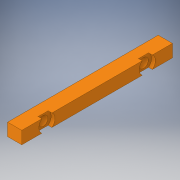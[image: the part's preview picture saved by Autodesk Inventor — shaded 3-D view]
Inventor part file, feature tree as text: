
AUTODESK INVENTOR PART (.ipt)
format: ipt  version: 2019 (Build 230136000, 136)  size: 123,904 bytes
history: native  units: in
note: dims shown in document units (in); Inventor stores cm internally (conversion verified against a paired STEP export)
features: sketch x3, extrude x2, hole x1
ambient origin geometry x8: Origin, YZ Plane, XZ Plane, XY Plane, X Axis, Y Axis, Z Axis, Center Point
bodies: Solid1 (feature_tree)
feature tree (6):
  extrude  "Extrusion1"  Depth=0.565in
  extrude  "Extrusion2"  Depth=0.5in
  hole  "Hole1"  [1 undecoded]
  sketch  "Sketch1"  dims[d0=6.0in d1=0.565in]
  sketch  "Sketch2"  dims[d2=0.5in d3=0.0in d4=0.375in]
  sketch  "Sketch4"  dims[d5=0.375in d6=4.0in d7=6.0in d8=1.0in d9=0.5in d10=0.25in d11=0.25in d12=0.5in d13=0.0in d43=0.64in d44=0.75in d45=0.375in d46=0.25in d47=0.5635in d48=0.15in d49=0.0in]
note: 1 required parameter value undecoded (feature->parameter linkage not recoverable at this tier; creation-order binding heuristic only, values carry confidence <= 0.55)
